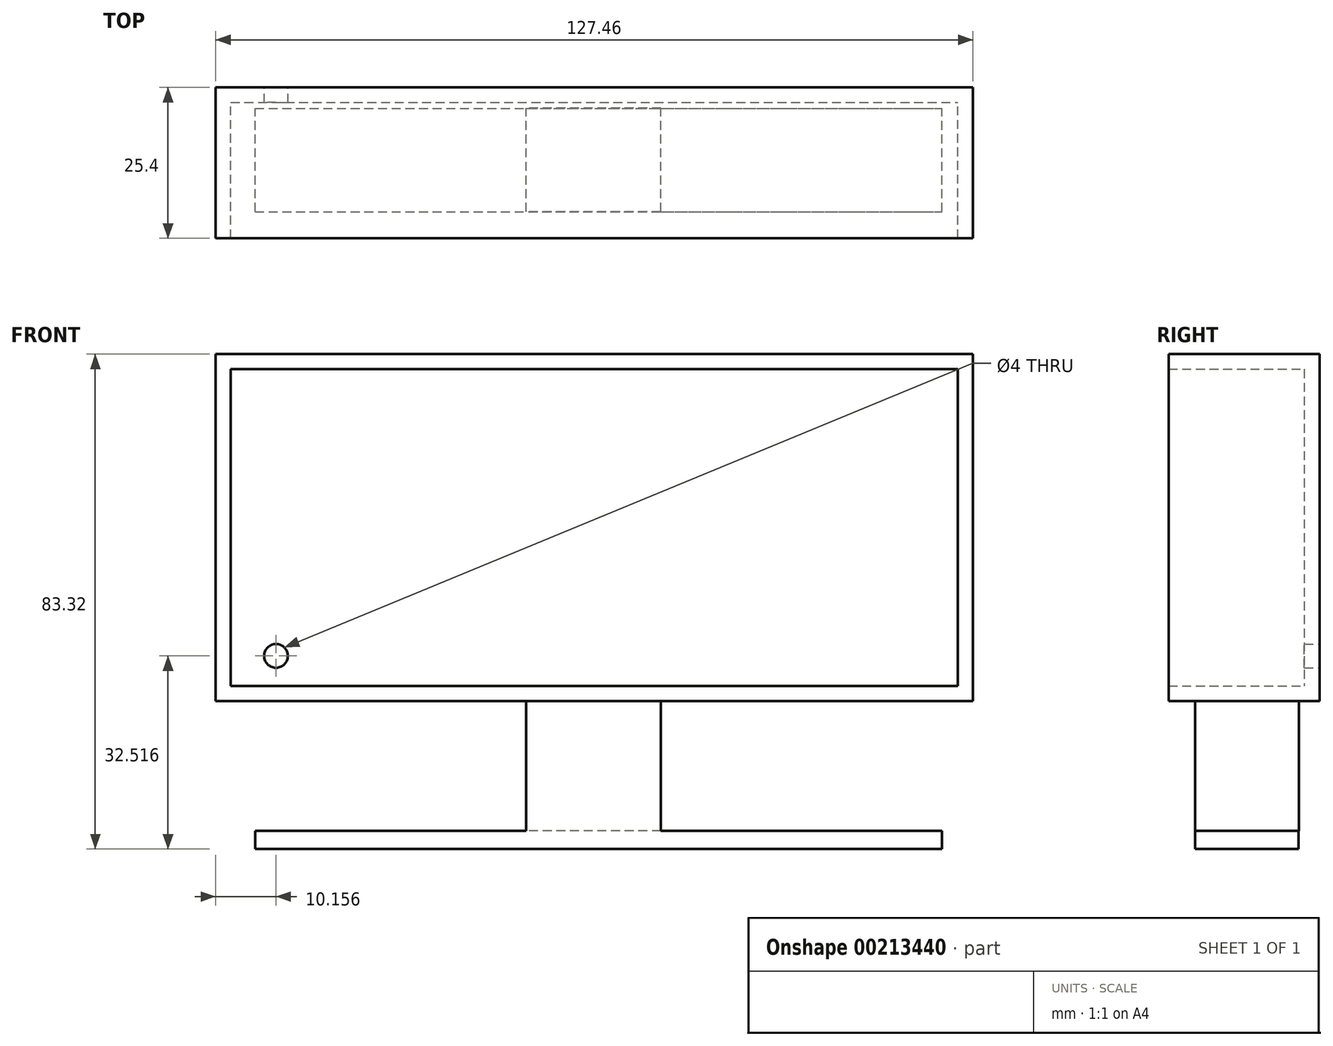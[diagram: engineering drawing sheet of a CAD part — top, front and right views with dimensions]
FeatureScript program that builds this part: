
annotation { "Feature Type Name" : "Feature", "Feature Type Description" : "" }
export const myFeature = defineFeature(function(context is Context, id is Id, definition is map)
    precondition{}
    {
        {
            var Q0;
            Q0=qCreatedBy(makeId("Front.planeOp"),FACE);
            var sketch = newSketch(context, id + "F0", { "sketchPlane" : qUnion([Q0])});
            skLineSegment(sketch, "E0.bottom", {"start": v(-61.88, 56) * mm, "end": v(65.58, 56) * mm});
            skLineSegment(sketch, "E0.top", {"start": v(-61.88, -2.42) * mm, "end": v(65.58, -2.42) * mm});
            skLineSegment(sketch, "E0.left", {"start": v(-61.88, 56) * mm, "end": v(-61.88, -2.42) * mm});
            skLineSegment(sketch, "E0.right", {"start": v(65.58, 56) * mm, "end": v(65.58, -2.42) * mm});
            skSolve(sketch);
        }
        {
            var Q0;
            Q0=makeQuery(id+"F0.imprint","IMPRINT",FACE,{"disambiguationData":[TD([[makeQuery(id+"F0.imprint","IMPRINT",EDGE,{"derivedFrom":sQuery(id+"F0.wireOp",EDGE,"E0.bottom")}),-1.0]])]});
            extrude(context, id + "F1", {"entities" : qUnion([Q0]), "depth" : 25.4 * mm});
        }
        {
            var Q0;
            Q0=makeQuery(id+"F1.opExtrude","CAP_FACE",FACE,{"disambiguationData":[OSD([sQuery(id+"F0.wireOp",EDGE,"E0.bottom"),sQuery(id+"F0.wireOp",EDGE,"E0.top"),sQuery(id+"F0.wireOp",EDGE,"E0.left"),sQuery(id+"F0.wireOp",EDGE,"E0.right")])],"isStart":false});
            shell(context, id + "F2", {"entities" : qUnion([Q0]), "thickness" : 2.54 * mm});
        }
        {
            var Q0;
            Q0=makeQuery(id+"F1.opExtrude","CAP_FACE",FACE,{"disambiguationData":[OSD([sQuery(id+"F0.wireOp",EDGE,"E0.bottom"),sQuery(id+"F0.wireOp",EDGE,"E0.top"),sQuery(id+"F0.wireOp",EDGE,"E0.left"),sQuery(id+"F0.wireOp",EDGE,"E0.right")])],"isStart":true});
            var sketch = newSketch(context, id + "F3", { "sketchPlane" : qUnion([Q0])});
            skPoint(sketch, "E1", {"position": v(51.72, 5.2) * mm});
            skSolve(sketch);
        }
        {
            var Q0;
            Q0=sQuery(id+"F3.wireOp",VERTEX,"E1");
            var Q1;
            Q1=makeQuery(id+"F1.opExtrude","SWEPT_BODY",BODY,{"disambiguationData":[OSD([sQuery(id+"F0.wireOp",EDGE,"E0.bottom"),sQuery(id+"F0.wireOp",EDGE,"E0.top"),sQuery(id+"F0.wireOp",EDGE,"E0.left"),sQuery(id+"F0.wireOp",EDGE,"E0.right")])]});
            hole(context, id + "F4", {"style" : HoleStyle.SIMPLE, "endStyle" : HoleEndStyle.THROUGH, "holeDiameter" : 4 * mm, "locations" : qUnion([Q0]), "scope" : qUnion([Q1]), "isTappedThrough" : true});
        }
        {
            var Q0;
            Q0=makeQuery(id+"F1.opExtrude","SWEPT_FACE",FACE,{"disambiguationData":[OSD([sQuery(id+"F0.wireOp",EDGE,"E0.top")])]});
            var sketch = newSketch(context, id + "F5", { "sketchPlane" : qUnion([Q0])});
            skLineSegment(sketch, "E2.bottom", {"start": v(13.06, 20.95) * mm, "end": v(-9.6, 20.95) * mm});
            skLineSegment(sketch, "E2.top", {"start": v(13.06, 3.48) * mm, "end": v(-9.6, 3.48) * mm});
            skLineSegment(sketch, "E2.left", {"start": v(13.06, 20.95) * mm, "end": v(13.06, 3.48) * mm});
            skLineSegment(sketch, "E2.right", {"start": v(-9.6, 20.95) * mm, "end": v(-9.6, 3.48) * mm});
            skSolve(sketch);
        }
        {
            var Q0;
            Q0=makeQuery(id+"F5.imprint","IMPRINT",FACE,{"disambiguationData":[TD([[makeQuery(id+"F5.imprint","IMPRINT",EDGE,{"derivedFrom":sQuery(id+"F5.wireOp",EDGE,"E2.bottom")}),1.0]])]});
            extrude(context, id + "F6", {"entities" : qUnion([Q0]), "operationType" : NewBodyOperationType.ADD, "depth" : 21.84 * mm});
        }
        {
            var Q0;
            Q0=makeQuery(id+"F6.opExtrude","CAP_FACE",FACE,{"disambiguationData":[OSD([sQuery(id+"F5.wireOp",EDGE,"E2.bottom"),sQuery(id+"F5.wireOp",EDGE,"E2.top"),sQuery(id+"F5.wireOp",EDGE,"E2.left"),sQuery(id+"F5.wireOp",EDGE,"E2.right")])],"isStart":false});
            var sketch = newSketch(context, id + "F7", { "sketchPlane" : qUnion([Q0])});
            skLineSegment(sketch, "E3.bottom", {"start": v(-55.25, 20.95) * mm, "end": v(60.33, 20.95) * mm});
            skLineSegment(sketch, "E3.top", {"start": v(-55.25, 3.54) * mm, "end": v(60.33, 3.54) * mm});
            skLineSegment(sketch, "E3.left", {"start": v(-55.25, 20.95) * mm, "end": v(-55.25, 3.54) * mm});
            skLineSegment(sketch, "E3.right", {"start": v(60.33, 20.95) * mm, "end": v(60.33, 3.54) * mm});
            skSolve(sketch);
        }
        {
            var Q0;
            {var subQ3=sQuery(id+"F7.wireOp",EDGE,"E3.right");Q0=makeQuery(id+"F7.imprint","IMPRINT",FACE,{"disambiguationData":[TD([[makeQuery(id+"F7.imprint","IMPRINT",EDGE,{"derivedFrom":subQ3}),-1.0]])]});}
            var Q1;
            {var subQ3=sQuery(id+"F7.wireOp",EDGE,"E3.left");Q1=makeQuery(id+"F7.imprint","IMPRINT",FACE,{"disambiguationData":[TD([[makeQuery(id+"F7.imprint","IMPRINT",EDGE,{"derivedFrom":subQ3}),1.0]])]});}
            var Q2;
            {var subQ0=sQuery(id+"F7.wireOp",EDGE,"E3.bottom");var subQ1=makeQuery(id+"F6.opExtrude","CAP_EDGE",EDGE,{"disambiguationData":[OSD([sQuery(id+"F5.wireOp",EDGE,"E2.left")])],"isStart":false});var subQ2=makeQuery(id+"F7.imprint","INTERSECT",VERTEX,{"derivedFrom":[subQ1,subQ0]});var subQ3=makeQuery(id+"F6.opExtrude","CAP_EDGE",EDGE,{"disambiguationData":[OSD([sQuery(id+"F5.wireOp",EDGE,"E2.right")])],"isStart":false});var subQ4=makeQuery(id+"F7.imprint","INTERSECT",VERTEX,{"derivedFrom":[subQ3,subQ0]});Q2=makeQuery(id+"F7.imprint","IMPRINT",FACE,{"disambiguationData":[TD([[makeQuery(id+"F7.imprint","IMPRINT",EDGE,{"disambiguationData":[TD([[subQ2,-1.0],[subQ4,1.0]])],"derivedFrom":subQ0}),1.0]])]});}
            extrude(context, id + "F8", {"entities" : qUnion([Q0, Q1, Q2]), "operationType" : NewBodyOperationType.ADD, "depth" : 3.05 * mm});
        }
    });
